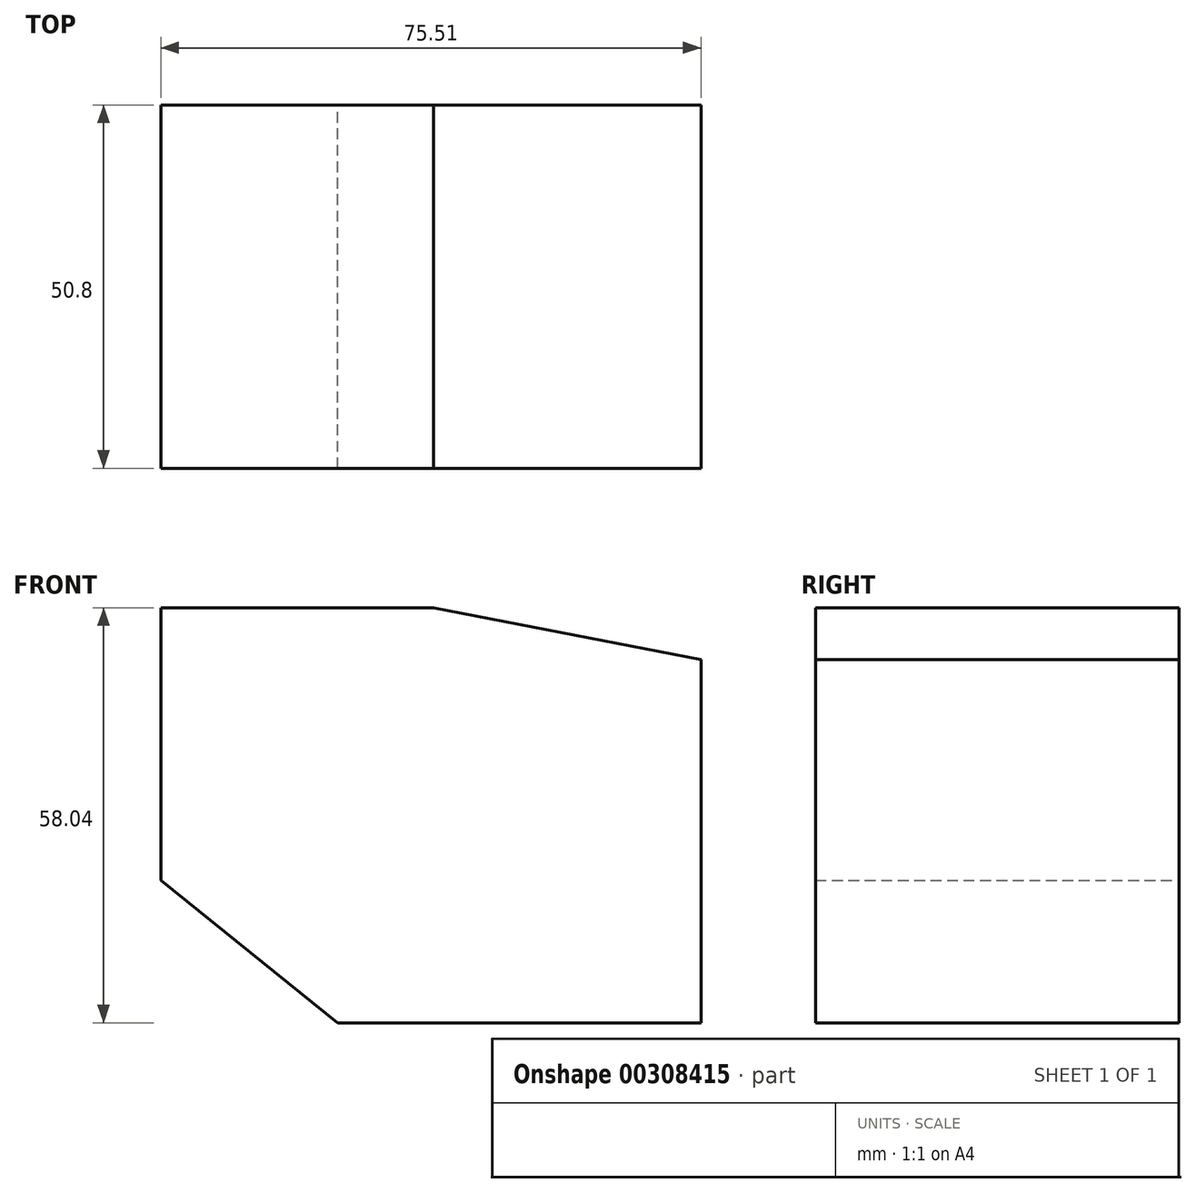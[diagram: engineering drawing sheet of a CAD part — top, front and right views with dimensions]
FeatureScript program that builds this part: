
annotation { "Feature Type Name" : "Feature", "Feature Type Description" : "" }
export const myFeature = defineFeature(function(context is Context, id is Id, definition is map)
    precondition{}
    {
        {
            var Q0;
            Q0=qCreatedBy(makeId("Front.planeOp"),FACE);
            var sketch = newSketch(context, id + "F0", { "sketchPlane" : qUnion([Q0])});
            skLineSegment(sketch, "E0", {"start": v(0, 0) * mm, "end": v(24.7, -19.94) * mm});
            skLineSegment(sketch, "E1", {"start": v(24.7, -19.94) * mm, "end": v(75.5, -19.94) * mm});
            skLineSegment(sketch, "E2", {"start": v(75.5, -19.94) * mm, "end": v(75.5, 30.86) * mm});
            skLineSegment(sketch, "E3", {"start": v(75.5, 30.86) * mm, "end": v(38.1, 38.1) * mm});
            skLineSegment(sketch, "E4", {"start": v(38.1, 38.1) * mm, "end": v(0, 38.1) * mm});
            skLineSegment(sketch, "E5", {"start": v(0, 38.1) * mm, "end": v(0, 0) * mm});
            skSolve(sketch);
        }
        {
            var Q0;
            Q0=makeQuery(id+"F0.imprint","IMPRINT",FACE,{"disambiguationData":[TD([[makeQuery(id+"F0.imprint","IMPRINT",EDGE,{"derivedFrom":sQuery(id+"F0.wireOp",EDGE,"E0")}),1.0]])]});
            extrude(context, id + "F1", {"entities" : qUnion([Q0]), "depth" : 50.8 * mm});
        }
    });
